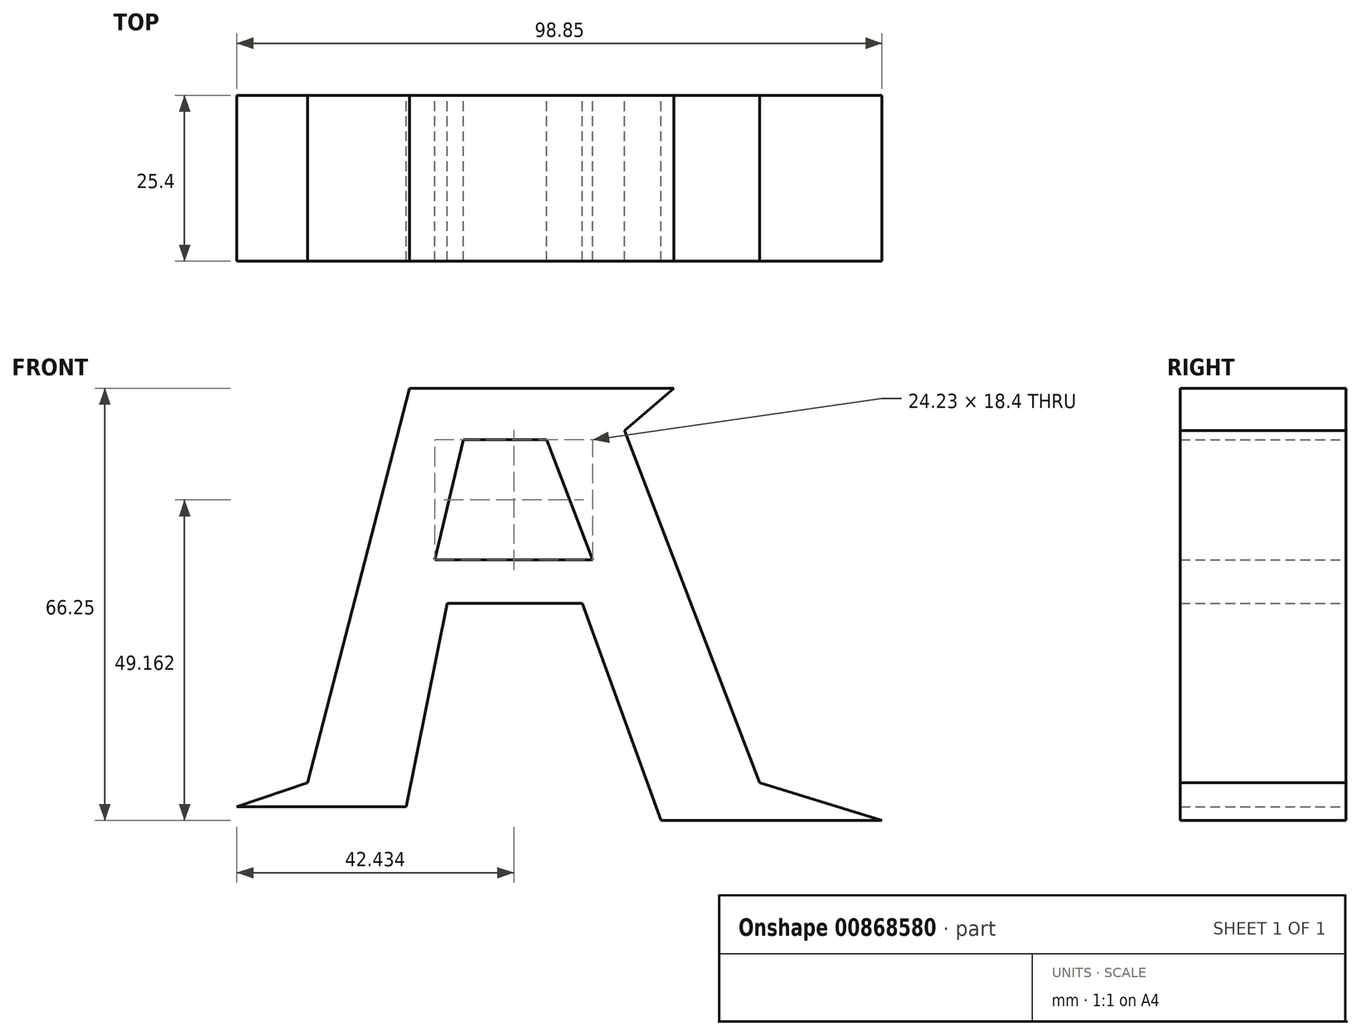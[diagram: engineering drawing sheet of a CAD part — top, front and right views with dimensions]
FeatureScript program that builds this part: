
annotation { "Feature Type Name" : "Feature", "Feature Type Description" : "" }
export const myFeature = defineFeature(function(context is Context, id is Id, definition is map)
    precondition{}
    {
        {
            var Q0;
            Q0=qCreatedBy(makeId("Front.planeOp"),FACE);
            var sketch = newSketch(context, id + "F0", { "sketchPlane" : qUnion([Q0])});
            skLineSegment(sketch, "E0", {"start": v(-18.5, -31.2) * mm, "end": v(-44.43, -31.2) * mm});
            skLineSegment(sketch, "E1", {"start": v(-44.43, -31.2) * mm, "end": v(-33.56, -27.52) * mm});
            skLineSegment(sketch, "E2", {"start": v(-33.56, -27.52) * mm, "end": v(-17.97, 32.95) * mm});
            skLineSegment(sketch, "E3", {"start": v(-17.97, 32.95) * mm, "end": v(22.52, 32.95) * mm});
            skLineSegment(sketch, "E4", {"start": v(22.52, 32.95) * mm, "end": v(14.99, 26.47) * mm});
            skLineSegment(sketch, "E5", {"start": v(14.99, 26.47) * mm, "end": v(35.67, -27.52) * mm});
            skLineSegment(sketch, "E6", {"start": v(35.67, -27.52) * mm, "end": v(54.42, -33.3) * mm});
            skLineSegment(sketch, "E7", {"start": v(54.42, -33.3) * mm, "end": v(20.6, -33.3) * mm});
            skLineSegment(sketch, "E8", {"start": v(20.6, -33.3) * mm, "end": v(8.5, 0) * mm});
            skLineSegment(sketch, "E9", {"start": v(8.5, 0) * mm, "end": v(-12.18, 0) * mm});
            skLineSegment(sketch, "E10", {"start": v(-12.18, 0) * mm, "end": v(-18.5, -31.2) * mm});
            skLineSegment(sketch, "E11", {"start": v(3.07, 25.06) * mm, "end": v(7.65, 13.1) * mm});
            skLineSegment(sketch, "E12", {"start": v(7.65, 13.1) * mm, "end": v(10.12, 6.66) * mm});
            skLineSegment(sketch, "E13", {"start": v(10.12, 6.66) * mm, "end": v(-14.1, 6.66) * mm});
            skLineSegment(sketch, "E14", {"start": v(-14.1, 6.66) * mm, "end": v(-9.73, 25.06) * mm});
            skPoint(sketch, "E15.start.orphan", {"position": v(-8.15, 25.06) * mm});
            skLineSegment(sketch, "E16", {"start": v(-9.73, 25.06) * mm, "end": v(3.07, 25.06) * mm});
            skSolve(sketch);
        }
        {
            var Q0;
            Q0=makeQuery(id+"F0.imprint","IMPRINT",FACE,{"disambiguationData":[TD([[makeQuery(id+"F0.imprint","IMPRINT",EDGE,{"derivedFrom":sQuery(id+"F0.wireOp",EDGE,"E0")}),-1.0]])]});
            extrude(context, id + "F1", {"entities" : qUnion([Q0]), "depth" : 25.4 * mm, "offsetDistance" : 25.4 * mm});
        }
    });
